# Revit family: Haworth_Pergola_Accessory_Tray_PRELIM
name_source: partatom
category: Furniture Systems
revit_build: Autodesk Revit 2018 (Build: 20170223_1515(x64)
units: mm (PartAtom-declared; Revit-internal decimal feet)

## family parameters
Always vertical = Yes
Cut with Voids When Loaded = No
OmniClass Number = 23.40.70.14.64.21
OmniClass Title = Systems Furniture
Part Type = Normal
Room Calculation Point = No
Round Connector Dimension = Use Diameter
Shared = No
Work Plane-Based = No

## types (3) — shared parameters
Actual Depth = 5 1/2"
Actual Height = 15/128"
Assembly Code = E2020200
Description = Haworth - Pergola Tray
Manufacturer = Haworth
Model = Haworth Pergola
Revision Number = 1
Size = Verify Final Dim. w/ Haworth
Standard Width = 18, 30, 42 in.
Sustainability Info = http://www.haworth.com
Trim Finish = Haworth _ Laminate _ Undecided _ Pergola
URL = http://www.haworth.com
URL - Product = https://www.haworth.com
Warranty = http://www.haworth.com

## per-type parameters (varying)
| type | Actual Width | Large - 42w | Medium - 30w | Small - 18w |
| 18w | 18" | No | No | Yes |
| 30w | 30" | No | Yes | No |
| 42w | 42" | Yes | No | No |

## geometry (parser evidence)
native form markers: Sweep x3
no freeform markers — native parametric forms only
